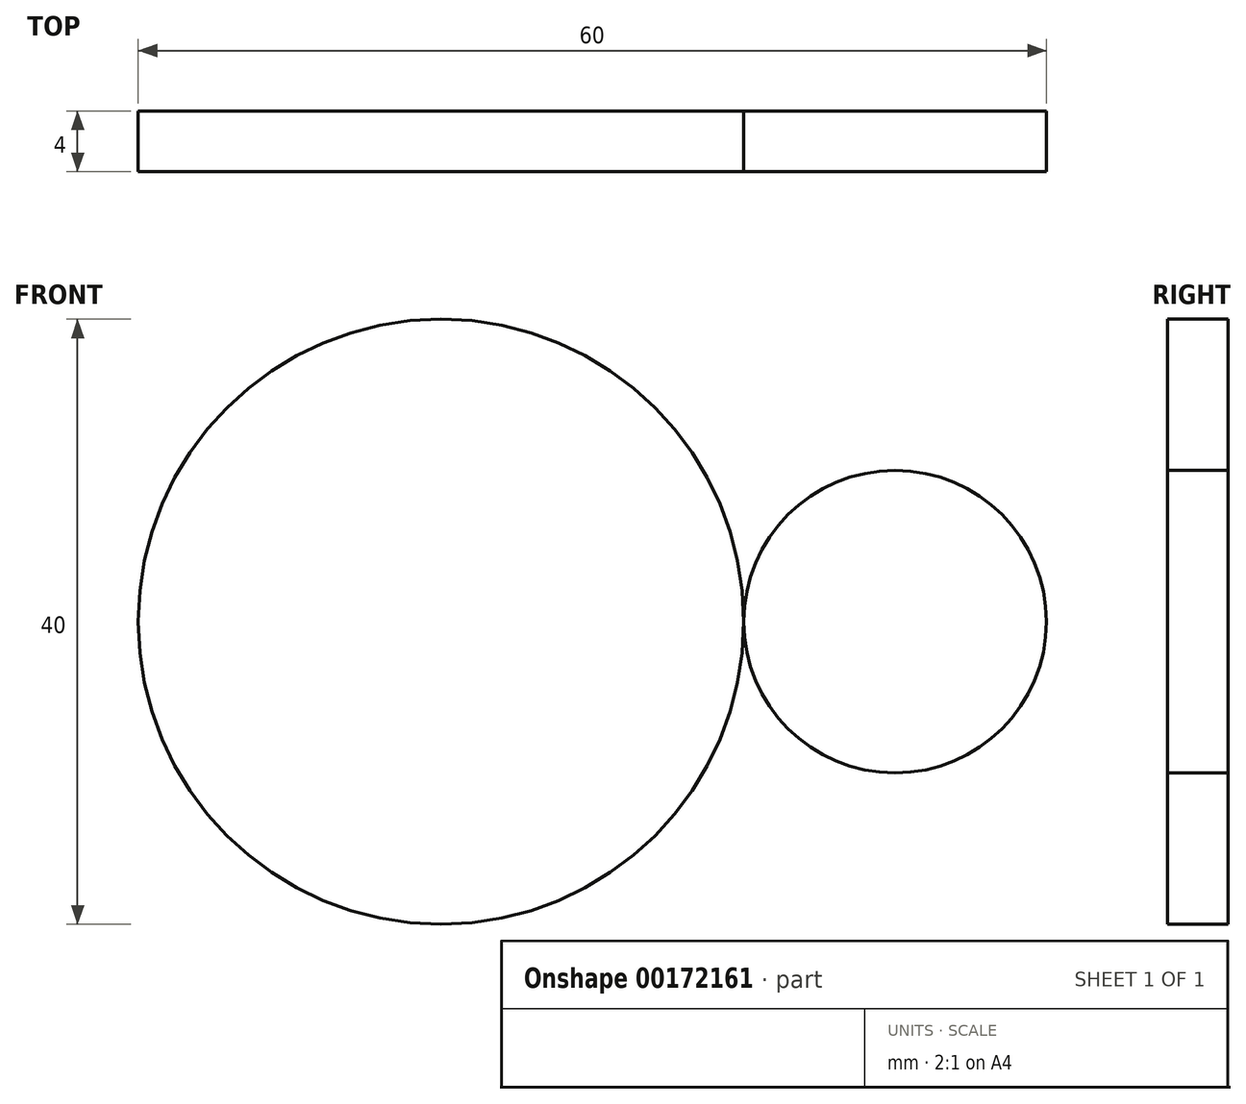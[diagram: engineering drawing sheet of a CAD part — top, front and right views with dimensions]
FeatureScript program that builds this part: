
annotation { "Feature Type Name" : "Feature", "Feature Type Description" : "" }
export const myFeature = defineFeature(function(context is Context, id is Id, definition is map)
    precondition{}
    {
        {
            var Q0;
            Q0=qCreatedBy(makeId("Front.planeOp"),FACE);
            var sketch = newSketch(context, id + "F0", { "sketchPlane" : qUnion([Q0])});
            skCircle(sketch, "E0", {"center": v(-49.5, 162.56) * mm, "radius": 20 * mm});
            skCircle(sketch, "E1", {"center": v(-19.5, 162.56) * mm, "radius": 10 * mm});
            skSolve(sketch);
        }
        {
            var Q0;
            Q0=makeQuery(id+"F0.imprint","IMPRINT",FACE,{"disambiguationData":[TD([[makeQuery(id+"F0.imprint","IMPRINT",EDGE,{"derivedFrom":sQuery(id+"F0.wireOp",EDGE,"E0")}),1.0]])]});
            var Q1;
            Q1=makeQuery(id+"F0.imprint","IMPRINT",FACE,{"disambiguationData":[TD([[makeQuery(id+"F0.imprint","IMPRINT",EDGE,{"derivedFrom":sQuery(id+"F0.wireOp",EDGE,"E1")}),1.0]])]});
            extrude(context, id + "F1", {"entities" : qUnion([Q0, Q1]), "depth" : 4 * mm});
        }
    });
